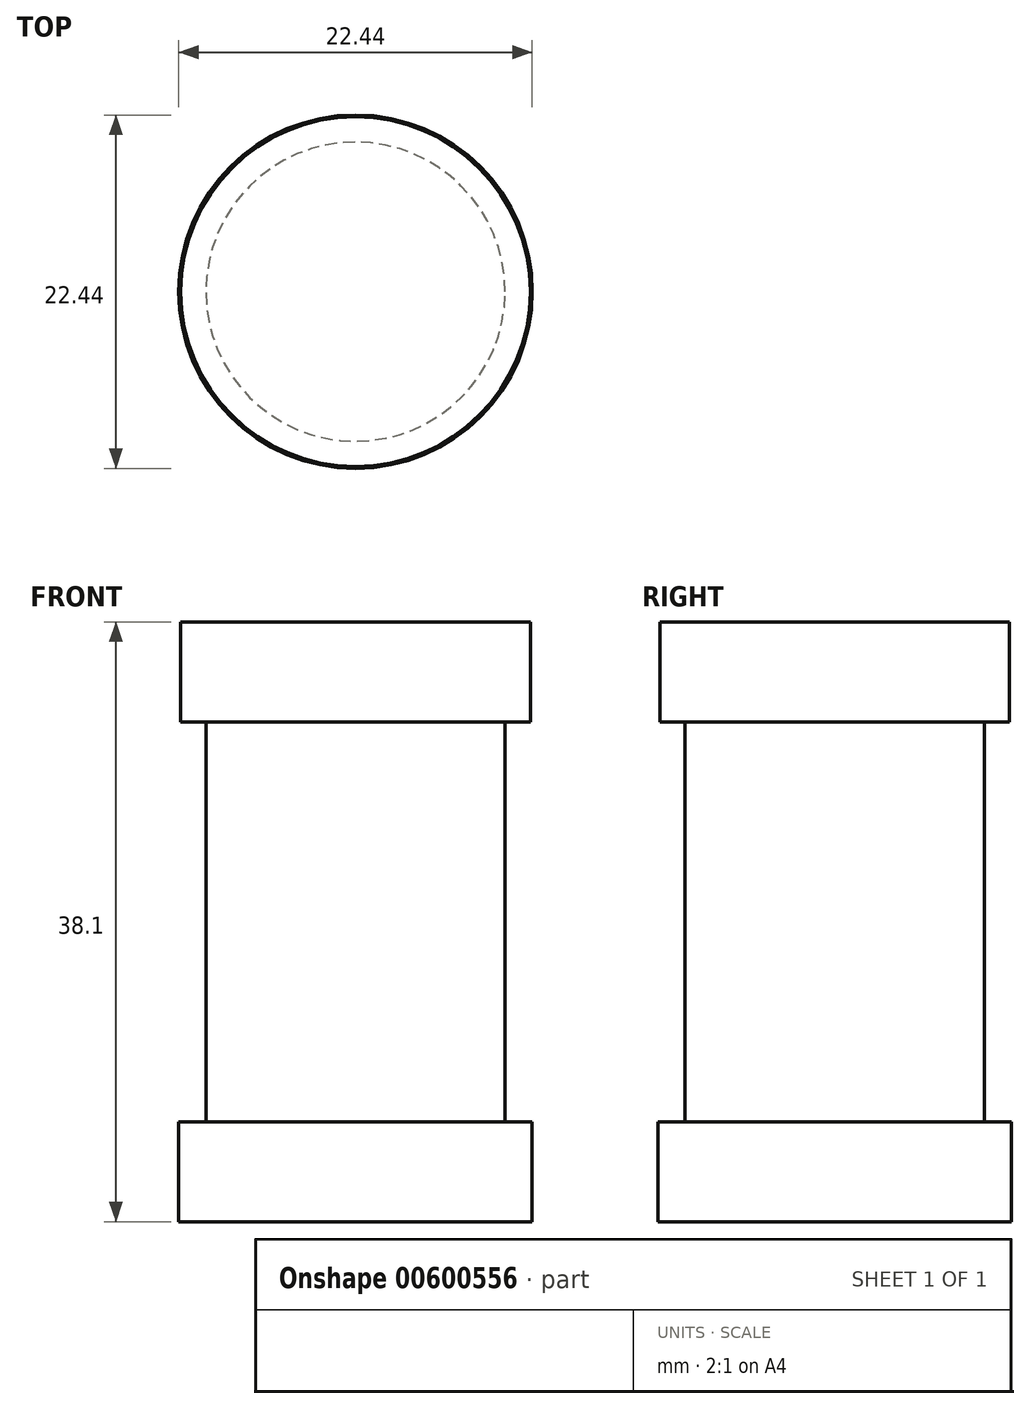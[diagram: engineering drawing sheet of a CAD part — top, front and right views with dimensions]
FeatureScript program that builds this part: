
annotation { "Feature Type Name" : "Feature", "Feature Type Description" : "" }
export const myFeature = defineFeature(function(context is Context, id is Id, definition is map)
    precondition{}
    {
        {
            var Q0;
            Q0=qCreatedBy(makeId("Top.planeOp"),FACE);
            var sketch = newSketch(context, id + "F0", { "sketchPlane" : qUnion([Q0])});
            skCircle(sketch, "E0", {"center": v(0, 0) * mm, "radius": 11.2 * mm});
            skSolve(sketch);
        }
        {
            var Q0;
            Q0=makeQuery(id+"F0.imprint","IMPRINT",FACE,{"disambiguationData":[TD([[makeQuery(id+"F0.imprint","IMPRINT",EDGE,{"derivedFrom":sQuery(id+"F0.wireOp",EDGE,"E0")}),1.0]])]});
            var Q1;
            Q1 = qSketchRegion(id + "F0", true);
            extrude(context, id + "F1", {"entities" : qUnion([Q0, Q1]), "depth" : 6.35 * mm, "offsetDistance" : 25.4 * mm});
        }
        {
            var Q0;
            Q0=makeQuery(id+"F1.opExtrude","CAP_FACE",FACE,{"disambiguationData":[OSD([sQuery(id+"F0.wireOp",EDGE,"E0")])],"isStart":false});
            var sketch = newSketch(context, id + "F2", { "sketchPlane" : qUnion([Q0])});
            skCircle(sketch, "E1", {"center": v(0, 0) * mm, "radius": 9.5 * mm});
            skSolve(sketch);
        }
        {
            var Q0;
            Q0 = qSketchRegion(id + "F2", true);
            extrude(context, id + "F3", {"entities" : qUnion([Q0]), "operationType" : NewBodyOperationType.ADD, "depth" : 25.4 * mm, "offsetDistance" : 25.4 * mm});
        }
        {
            var Q0;
            Q0=qCreatedBy(makeId("Top.planeOp"),FACE);
            var sketch = newSketch(context, id + "F4", { "sketchPlane" : qUnion([Q0])});
            skCircle(sketch, "E2", {"center": v(0, 0) * mm, "radius": 11.22 * mm});
            skSolve(sketch);
        }
        {
            var Q0;
            Q0 = qSketchRegion(id + "F4", true);
            extrude(context, id + "F5", {"entities" : qUnion([Q0]), "operationType" : NewBodyOperationType.ADD, "depth" : 6.35 * mm, "offsetDistance" : 25.4 * mm});
        }
        {
            var Q0;
            Q0=makeQuery(id+"F3.opExtrude","CAP_FACE",FACE,{"disambiguationData":[OSD([sQuery(id+"F2.wireOp",EDGE,"E1")])],"isStart":false});
            var sketch = newSketch(context, id + "F6", { "sketchPlane" : qUnion([Q0])});
            skCircle(sketch, "E3", {"center": v(0, 0) * mm, "radius": 11.1 * mm});
            skSolve(sketch);
        }
        {
            var Q0;
            Q0 = qSketchRegion(id + "F6", true);
            extrude(context, id + "F7", {"entities" : qUnion([Q0]), "operationType" : NewBodyOperationType.ADD, "depth" : 6.35 * mm, "offsetDistance" : 25.4 * mm});
        }
        {
            var Q0;
            Q0=makeQuery(id+"F7.opExtrude","CAP_FACE",FACE,{"disambiguationData":[OSD([sQuery(id+"F6.wireOp",EDGE,"E3")])],"isStart":false});
            var sketch = newSketch(context, id + "F8", { "sketchPlane" : qUnion([Q0])});
            skCircle(sketch, "E4", {"center": v(0, 0) * mm, "radius": 10.25 * mm});
            skSolve(sketch);
        }
    });
